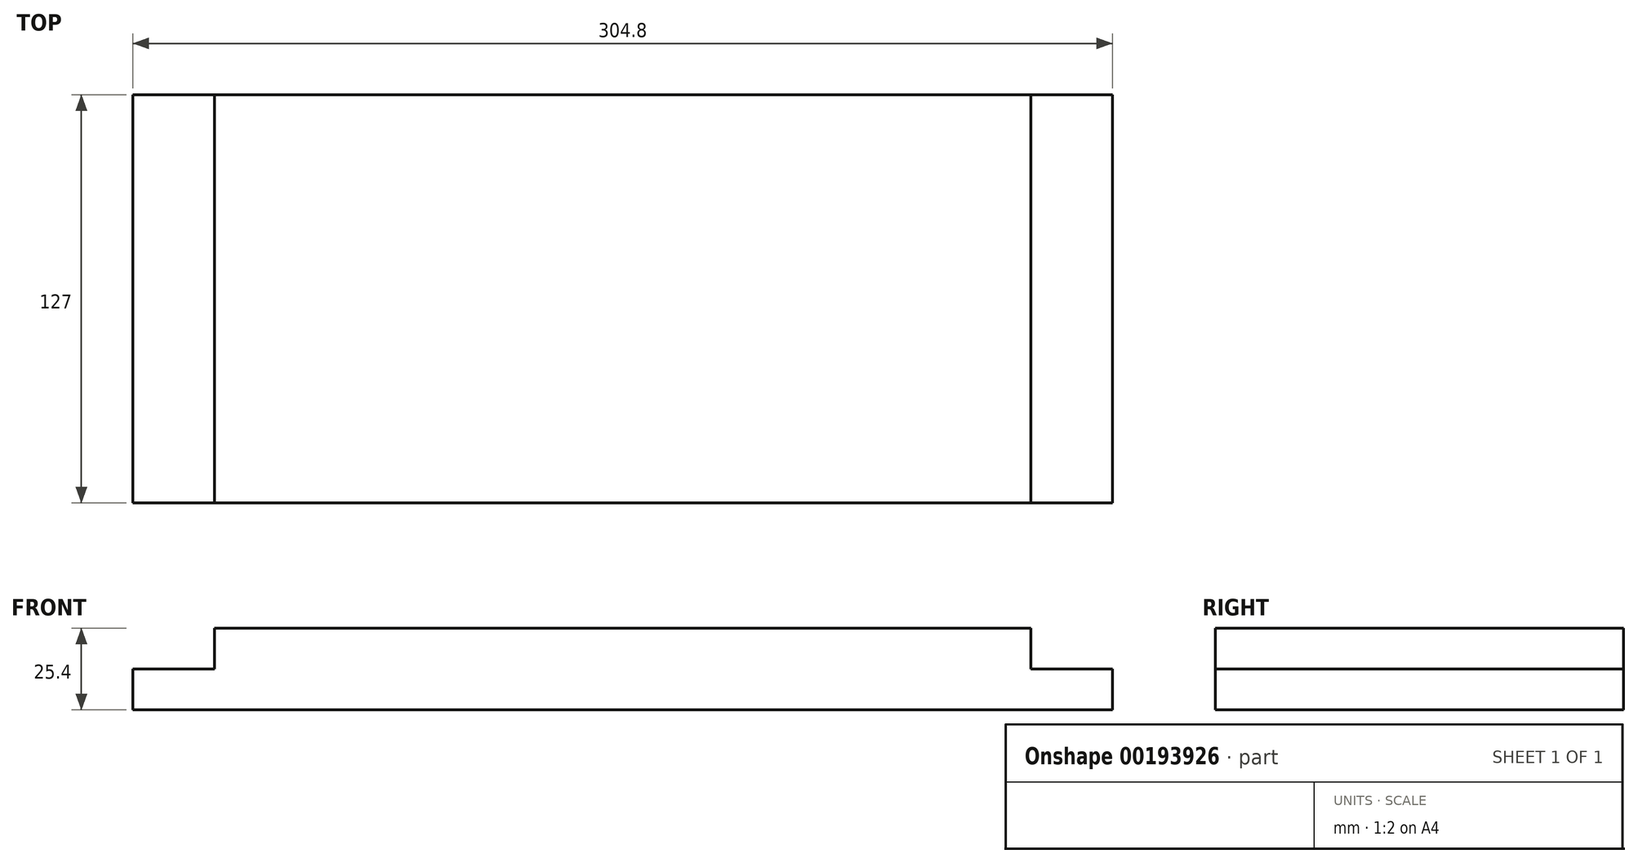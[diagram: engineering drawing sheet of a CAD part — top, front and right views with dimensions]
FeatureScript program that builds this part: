
annotation { "Feature Type Name" : "Feature", "Feature Type Description" : "" }
export const myFeature = defineFeature(function(context is Context, id is Id, definition is map)
    precondition{}
    {
        {
            var Q0;
            Q0=qCreatedBy(makeId("Top.planeOp"),FACE);
            var sketch = newSketch(context, id + "F0", { "sketchPlane" : qUnion([Q0])});
            skLineSegment(sketch, "E0.bottom", {"start": v(-155.06, 54.38) * mm, "end": v(149.74, 54.38) * mm});
            skLineSegment(sketch, "E0.top", {"start": v(-155.06, -98.02) * mm, "end": v(149.74, -98.02) * mm});
            skLineSegment(sketch, "E0.left", {"start": v(-155.06, 54.38) * mm, "end": v(-155.06, -98.02) * mm});
            skLineSegment(sketch, "E0.right", {"start": v(149.74, 54.38) * mm, "end": v(149.74, -98.02) * mm});
            skLineSegment(sketch, "E1.0", {"start": v(-129.66, 54.38) * mm, "end": v(-129.66, -98.02) * mm});
            skLineSegment(sketch, "E2.0", {"start": v(124.34, 54.38) * mm, "end": v(124.34, -98.02) * mm});
            skSolve(sketch);
        }
        {
            var Q0;
            {var subQ0=sQuery(id+"F0.wireOp",EDGE,"E1.0");Q0=makeQuery(id+"F0.imprint","IMPRINT",FACE,{"disambiguationData":[TD([[makeQuery(id+"F0.imprint","IMPRINT",EDGE,{"derivedFrom":subQ0}),1.0]])]});}
            extrude(context, id + "F1", {"entities" : qUnion([Q0]), "depth" : 25.4 * mm});
        }
        {
            var Q0;
            {var subQ0=sQuery(id+"F0.wireOp",EDGE,"E0.left");Q0=makeQuery(id+"F0.imprint","IMPRINT",FACE,{"disambiguationData":[TD([[makeQuery(id+"F0.imprint","IMPRINT",EDGE,{"derivedFrom":subQ0}),1.0]])]});}
            extrude(context, id + "F2", {"entities" : qUnion([Q0]), "operationType" : NewBodyOperationType.ADD, "depth" : 12.7 * mm});
        }
        {
            var Q0;
            Q0 = qSketchRegion(id + "F0", true);
            extrude(context, id + "F3", {"entities" : qUnion([Q0]), "operationType" : NewBodyOperationType.ADD, "depth" : 12.7 * mm});
        }
        {
            var Q0;
            {var subQ0=sQuery(id+"F0.wireOp",EDGE,"E0.left");var subQ1=sQuery(id+"F0.wireOp",EDGE,"E0.top");var subQ2=sQuery(id+"F0.wireOp",EDGE,"E0.bottom");var subQ3=sQuery(id+"F0.wireOp",EDGE,"E1.0");Q0=makeQuery(id+"F3.boolean.opBoolean","MERGE",FACE,{"derivedFrom":[makeQuery(id+"F2.boolean.opBoolean","MERGE",FACE,{"derivedFrom":[makeQuery(id+"F1.opExtrude","CAP_FACE",FACE,{"disambiguationData":[OSD([subQ2,subQ1,subQ3,sQuery(id+"F0.wireOp",EDGE,"E2.0")])],"isStart":true}),makeQuery(id+"F2.opExtrude","CAP_FACE",FACE,{"disambiguationData":[OSD([subQ2,subQ1,subQ0,subQ3])],"isStart":true})]}),makeQuery(id+"F3.opExtrude","CAP_FACE",FACE,{"disambiguationData":[OSD([subQ2,subQ1,subQ0,sQuery(id+"F0.wireOp",EDGE,"E0.right")])],"isStart":true})]});}
            var sketch = newSketch(context, id + "F4", { "sketchPlane" : qUnion([Q0])});
            skLineSegment(sketch, "E3.0", {"start": v(-155.06, 85.32) * mm, "end": v(149.74, 85.32) * mm});
            skLineSegment(sketch, "E4.0", {"start": v(-155.06, -41.68) * mm, "end": v(149.74, -41.68) * mm});
            skSolve(sketch);
        }
        {
            var Q0;
            {var subQ0=sQuery(id+"F4.wireOp",EDGE,"E3.0");Q0=makeQuery(id+"F4.imprint","IMPRINT",FACE,{"disambiguationData":[TD([[makeQuery(id+"F4.imprint","IMPRINT",EDGE,{"derivedFrom":subQ0}),1.0]])]});}
            var Q1;
            {var subQ0=sQuery(id+"F4.wireOp",EDGE,"E4.0");Q1=makeQuery(id+"F4.imprint","IMPRINT",FACE,{"disambiguationData":[TD([[makeQuery(id+"F4.imprint","IMPRINT",EDGE,{"derivedFrom":subQ0}),-1.0]])]});}
            extrude(context, id + "F5", {"entities" : qUnion([Q0, Q1]), "operationType" : NewBodyOperationType.REMOVE, "oppositeDirection" : true, "depth" : 152.4 * mm});
        }
    });
